# Revit family: Shower-Outlet-Dorf Epic Rain1
name_source: partatom
category: Plumbing Fixtures
revit_build: Autodesk Revit Architecture 2012 (Build: 20110916_2132(x64)
units: mm (PartAtom-declared; Revit-internal decimal feet)

## types (2) — shared parameters
Assembly Code = C1030210
CW Connection = Yes
CWFU = 2
Connector Radius = 10 mm  [stored 0.0328084 ft]
Description = Adjustable head, Simple, sleek design, Peace-of-mind with Dorf product warranty, Sure fit® installation
HW Connection = Yes
HWFU = 2
Manufacturer = Dorf
Material_ANZRS = Metal-Chrome-Caroma
URL = http://www.dorf.com.au
Vent Connection = No
Waste Connection = No
zero-valued in all types: Default Elevation

## per-type parameters (varying)
| type | Large | Length | Model | Type Comments |
| Epic Rain Showerhead with 200mm Arm | No | 200 mm | 6393.04 | Epic Ceiling Shower Arm 200mm |
| Epic Rain Showerhead with 400mm Arm | Yes | 400 mm  [stored 1.31234 ft] | 6394.04 | Epic Ceiling Shower Arm 400mm |

note: [stored X ft] marks values corroborated as IEEE doubles in the binary element streams (Revit-internal decimal feet)

## geometry (parser evidence)
native form markers: Blend x2, Sweep x4
no freeform markers — native parametric forms only
